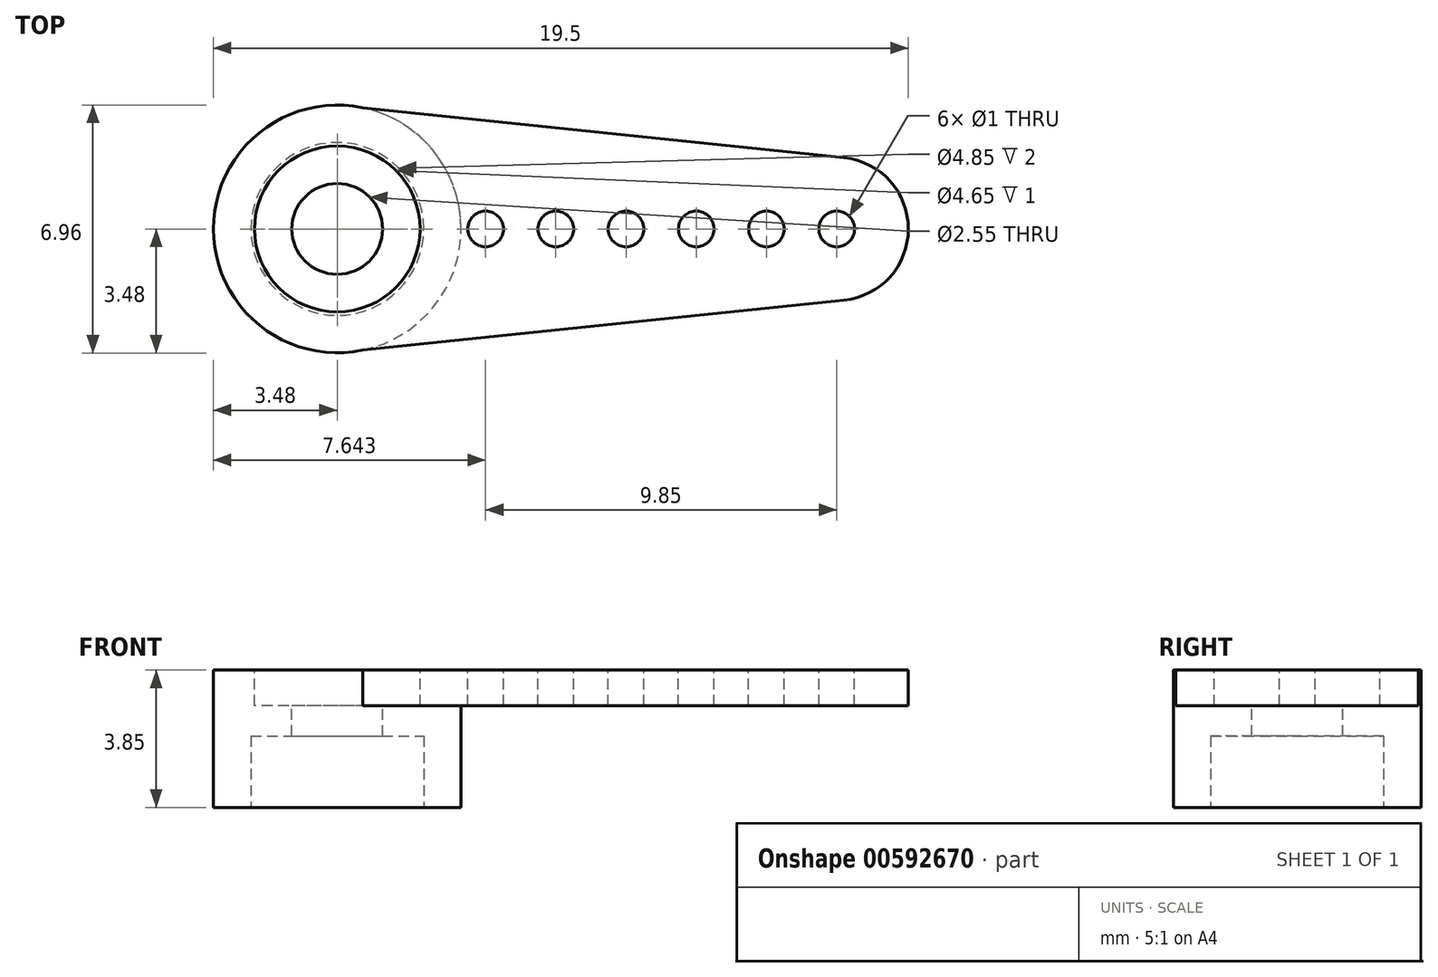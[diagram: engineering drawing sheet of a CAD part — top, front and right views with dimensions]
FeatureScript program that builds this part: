
annotation { "Feature Type Name" : "Feature", "Feature Type Description" : "" }
export const myFeature = defineFeature(function(context is Context, id is Id, definition is map)
    precondition{}
    {
        {
            var Q0;
            Q0=qCreatedBy(makeId("Top.planeOp"),FACE);
            var sketch = newSketch(context, id + "F0", { "sketchPlane" : qUnion([Q0])});
            skCircle(sketch, "E0", {"center": v(0, 0) * mm, "radius": 3.48 * mm});
            skSolve(sketch);
        }
        {
            var Q0;
            Q0=makeQuery(id+"F0.imprint","IMPRINT",FACE,{"disambiguationData":[TD([[makeQuery(id+"F0.imprint","IMPRINT",EDGE,{"derivedFrom":sQuery(id+"F0.wireOp",EDGE,"E0")}),1.0]])]});
            extrude(context, id + "F1", {"entities" : qUnion([Q0]), "depth" : 3.85 * mm, "offsetDistance" : 25 * mm});
        }
        {
            var Q0;
            Q0=makeQuery(id+"F1.opExtrude","CAP_FACE",FACE,{"disambiguationData":[OSD([sQuery(id+"F0.wireOp",EDGE,"E0")])],"isStart":true});
            var sketch = newSketch(context, id + "F2", { "sketchPlane" : qUnion([Q0])});
            skCircle(sketch, "E1", {"center": v(0, 0) * mm, "radius": 2.43 * mm});
            skSolve(sketch);
        }
        {
            var Q0;
            Q0 = qSketchRegion(id + "F2", true);
            extrude(context, id + "F3", {"entities" : qUnion([Q0]), "operationType" : NewBodyOperationType.REMOVE, "oppositeDirection" : true, "depth" : 2 * mm, "offsetDistance" : 25 * mm});
        }
        {
            var Q0;
            Q0=makeQuery(id+"F1.opExtrude","CAP_FACE",FACE,{"disambiguationData":[OSD([sQuery(id+"F0.wireOp",EDGE,"E0")])],"isStart":false});
            var sketch = newSketch(context, id + "F4", { "sketchPlane" : qUnion([Q0])});
            skArc(sketch, "E2.0", {"start": v(0, 3.48) * mm, "mid": v(-3.48, 0) * mm, "end": v(0, -3.48) * mm});
            skLineSegment(sketch, "E3", {"start": v(0, 3.47) * mm, "end": v(14.22, 2) * mm});
            skLineSegment(sketch, "E4", {"start": v(0, -3.48) * mm, "end": v(14.22, -2) * mm});
            skLineSegment(sketch, "E5", {"start": v(0, 0) * mm, "end": v(14.22, 0) * mm, "construction": true});
            skLineSegment(sketch, "E6", {"start": v(14.22, 2) * mm, "end": v(14.22, 0) * mm, "construction": true});
            skLineSegment(sketch, "E7", {"start": v(14.22, 0) * mm, "end": v(14.22, -2) * mm, "construction": true});
            skArc(sketch, "E8", {"start": v(14.22, 2) * mm, "mid": v(16.02, 0) * mm, "end": v(14.22, -2) * mm});
            skSolve(sketch);
        }
        {
            var Q0;
            Q0 = qSketchRegion(id + "F4", true);
            extrude(context, id + "F5", {"entities" : qUnion([Q0]), "operationType" : NewBodyOperationType.ADD, "oppositeDirection" : true, "depth" : 1 * mm, "offsetDistance" : 25 * mm});
        }
        {
            var Q0;
            Q0=makeQuery(id+"F5.boolean.opBoolean","MERGE",FACE,{"derivedFrom":[makeQuery(id+"F1.opExtrude","CAP_FACE",FACE,{"disambiguationData":[OSD([sQuery(id+"F0.wireOp",EDGE,"E0")])],"isStart":false}),makeQuery(id+"F5.opExtrude","CAP_FACE",FACE,{"disambiguationData":[OSD([sQuery(id+"F4.wireOp",EDGE,"E2.0"),sQuery(id+"F4.wireOp",EDGE,"E3"),sQuery(id+"F4.wireOp",EDGE,"E4"),sQuery(id+"F4.wireOp",EDGE,"E8")])],"isStart":true})]});
            var sketch = newSketch(context, id + "F6", { "sketchPlane" : qUnion([Q0])});
            skCircle(sketch, "E9", {"center": v(0, 0) * mm, "radius": 2.33 * mm});
            skSolve(sketch);
        }
        {
            var Q0;
            Q0 = qSketchRegion(id + "F6", true);
            extrude(context, id + "F7", {"entities" : qUnion([Q0]), "operationType" : NewBodyOperationType.REMOVE, "oppositeDirection" : true, "depth" : 1 * mm, "offsetDistance" : 25 * mm});
        }
        {
            var Q0;
            Q0=makeQuery(id+"F7.boolean.opBoolean","COPY",FACE,{"derivedFrom":makeQuery(id+"F7.opExtrude","CAP_FACE",FACE,{"disambiguationData":[OSD([sQuery(id+"F6.wireOp",EDGE,"E9")])],"isStart":false})});
            var sketch = newSketch(context, id + "F8", { "sketchPlane" : qUnion([Q0])});
            skCircle(sketch, "E10", {"center": v(0, 0) * mm, "radius": 1.27 * mm});
            skSolve(sketch);
        }
        {
            var Q0;
            Q0 = qSketchRegion(id + "F8", true);
            extrude(context, id + "F9", {"entities" : qUnion([Q0]), "operationType" : NewBodyOperationType.REMOVE, "endBound" : BoundingType.THROUGH_ALL, "oppositeDirection" : true, "depth" : 25 * mm, "offsetDistance" : 25 * mm});
        }
        {
            var Q0;
            Q0=makeQuery(id+"F5.boolean.opBoolean","MERGE",FACE,{"derivedFrom":[makeQuery(id+"F1.opExtrude","CAP_FACE",FACE,{"disambiguationData":[OSD([sQuery(id+"F0.wireOp",EDGE,"E0")])],"isStart":false}),makeQuery(id+"F5.opExtrude","CAP_FACE",FACE,{"disambiguationData":[OSD([sQuery(id+"F4.wireOp",EDGE,"E2.0"),sQuery(id+"F4.wireOp",EDGE,"E3"),sQuery(id+"F4.wireOp",EDGE,"E4"),sQuery(id+"F4.wireOp",EDGE,"E8")])],"isStart":true})]});
            var sketch = newSketch(context, id + "F10", { "sketchPlane" : qUnion([Q0])});
            skCircle(sketch, "E11", {"center": v(14.01, 0) * mm, "radius": 0.5 * mm});
            skCircle(sketch, "E12.1.0.0", {"center": v(12.04, 0) * mm, "radius": 0.5 * mm});
            skCircle(sketch, "E12.2.0.0", {"center": v(10.07, 0) * mm, "radius": 0.5 * mm});
            skCircle(sketch, "E12.3.0.0", {"center": v(8.1, 0) * mm, "radius": 0.5 * mm});
            skCircle(sketch, "E12.4.0.0", {"center": v(6.13, 0) * mm, "radius": 0.5 * mm});
            skCircle(sketch, "E12.5.0.0", {"center": v(4.16, 0) * mm, "radius": 0.5 * mm});
            skLineSegment(sketch, "E12.direction1", {"start": v(14.01, 0) * mm, "end": v(12.04, 0) * mm, "construction": true});
            skSolve(sketch);
        }
        {
            var Q0;
            Q0 = qSketchRegion(id + "F10", true);
            extrude(context, id + "F11", {"entities" : qUnion([Q0]), "operationType" : NewBodyOperationType.REMOVE, "endBound" : BoundingType.THROUGH_ALL, "oppositeDirection" : true, "depth" : 25 * mm, "offsetDistance" : 25 * mm});
        }
    });
